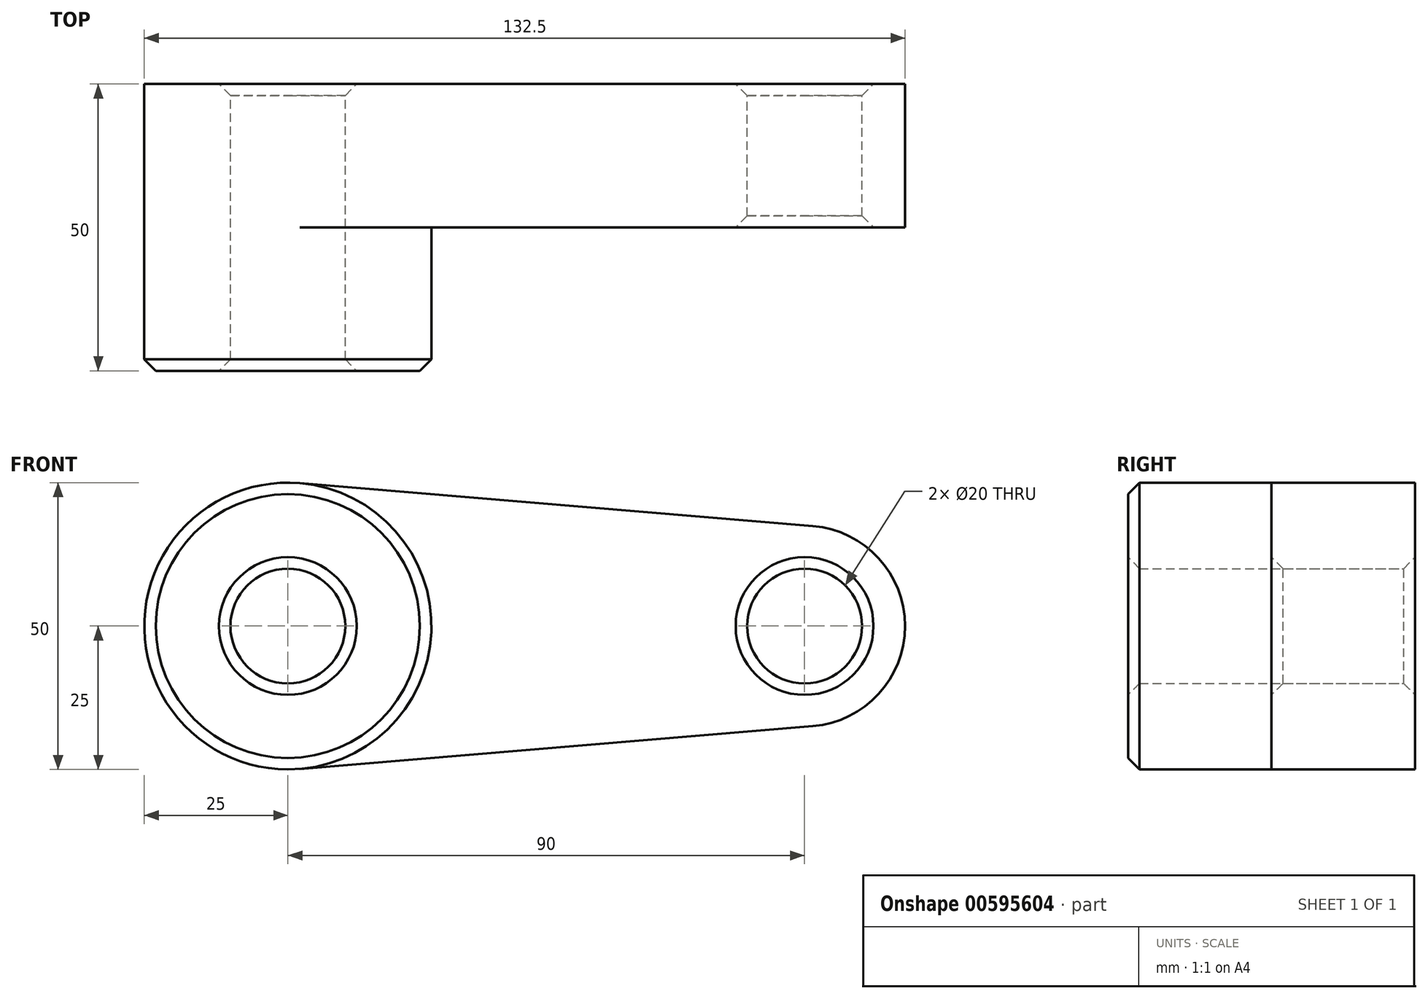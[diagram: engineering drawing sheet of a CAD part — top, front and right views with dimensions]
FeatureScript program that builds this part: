
annotation { "Feature Type Name" : "Feature", "Feature Type Description" : "" }
export const myFeature = defineFeature(function(context is Context, id is Id, definition is map)
    precondition{}
    {
        {
            var Q0;
            Q0=qCreatedBy(makeId("Front.planeOp"),FACE);
            var sketch = newSketch(context, id + "F0", { "sketchPlane" : qUnion([Q0])});
            skCircle(sketch, "E0", {"center": v(0, 0) * mm, "radius": 25 * mm});
            skCircle(sketch, "E1", {"center": v(90, 0) * mm, "radius": 17.5 * mm});
            skLineSegment(sketch, "E2", {"start": v(2.08, 24.91) * mm, "end": v(91.46, 17.44) * mm});
            skLineSegment(sketch, "E3", {"start": v(2.08, -24.91) * mm, "end": v(91.46, -17.44) * mm});
            skCircle(sketch, "E4", {"center": v(0, 0) * mm, "radius": 10 * mm});
            skCircle(sketch, "E5", {"center": v(90, 0) * mm, "radius": 10 * mm});
            skSolve(sketch);
        }
        {
            var Q0;
            Q0=qSketchRegion(id+"F0",true);
            extrude(context, id + "F1", {"entities" : qUnion([Q0]), "depth" : 25 * mm});
        }
        {
            var Q0;
            Q0=makeQuery(id+"F0.imprint","IMPRINT",FACE,{"disambiguationData":[TD([[makeQuery(id+"F0.imprint","IMPRINT",EDGE,{"derivedFrom":sQuery(id+"F0.wireOp",EDGE,"E4")}),-1.0]])]});
            extrude(context, id + "F2", {"entities" : qUnion([Q0]), "operationType" : NewBodyOperationType.ADD, "depth" : 50 * mm});
        }
        {
            var Q0;
            Q0=makeQuery(id+"F2.opExtrude","CAP_EDGE",EDGE,{"disambiguationData":[OSD([sQuery(id+"F0.wireOp",EDGE,"E0")])],"isStart":false});
            var Q1;
            Q1=makeQuery(id+"F2.opExtrude","CAP_EDGE",EDGE,{"disambiguationData":[OSD([sQuery(id+"F0.wireOp",EDGE,"E4")])],"isStart":false});
            var Q2;
            Q2=makeQuery(id+"F1.opExtrude","CAP_EDGE",EDGE,{"disambiguationData":[OSD([sQuery(id+"F0.wireOp",EDGE,"E5")])],"isStart":false});
            chamfer(context, id + "F3", {"entities" : qUnion([Q0, Q1, Q2]), "width" : 2 * mm, "tangentPropagation" : true});
        }
        {
            var Q0;
            Q0=makeQuery(id+"F1.opExtrude","CAP_EDGE",EDGE,{"disambiguationData":[OSD([sQuery(id+"F0.wireOp",EDGE,"E5")])],"isStart":true});
            var Q1;
            Q1=makeQuery(id+"F1.opExtrude","CAP_EDGE",EDGE,{"disambiguationData":[OSD([sQuery(id+"F0.wireOp",EDGE,"E4")])],"isStart":true});
            chamfer(context, id + "F4", {"entities" : qUnion([Q0, Q1]), "width" : 2 * mm, "tangentPropagation" : true});
        }
    });
